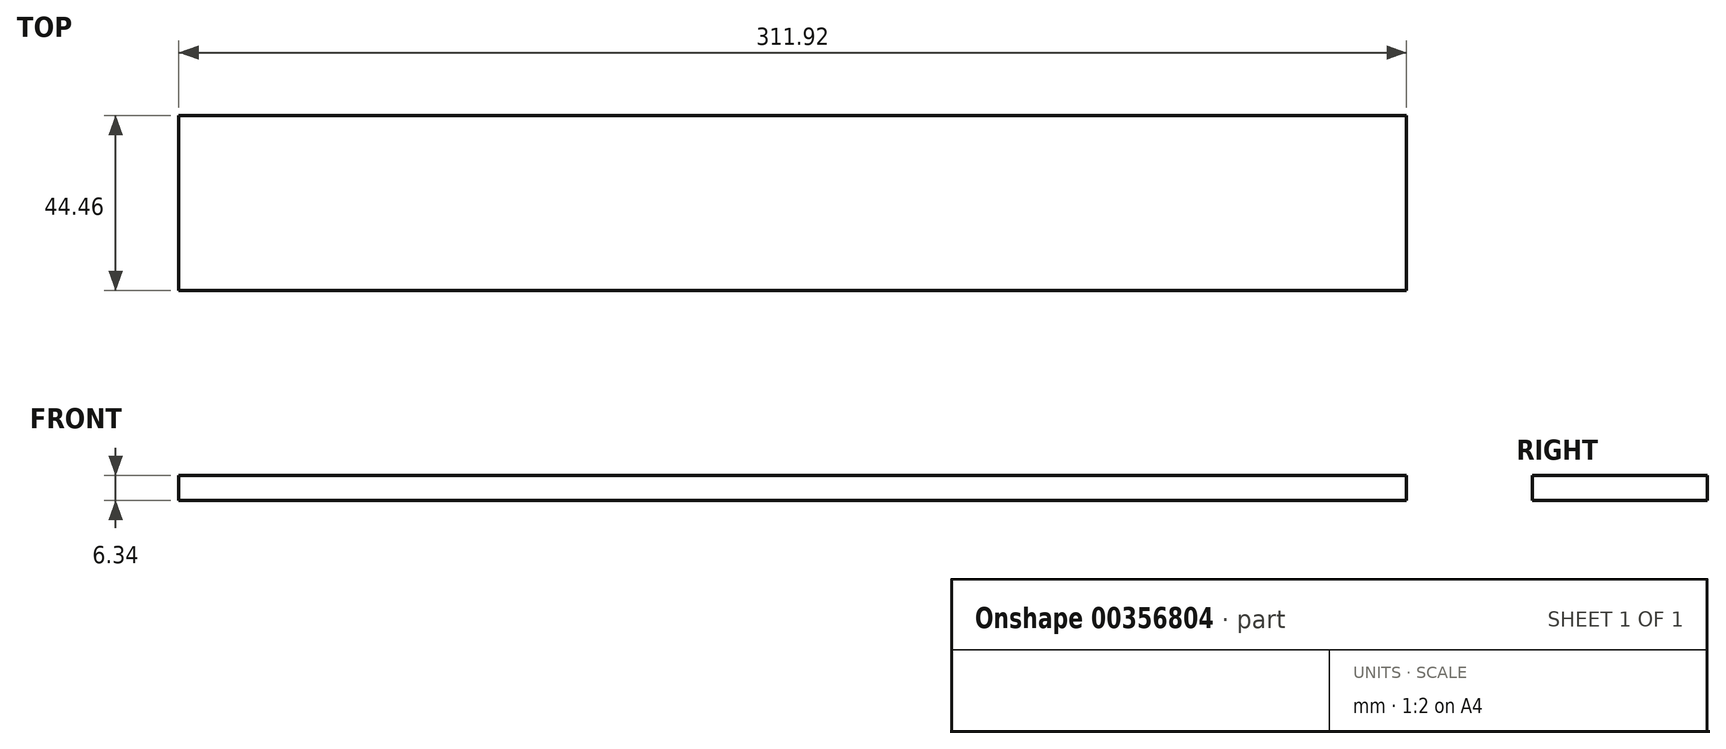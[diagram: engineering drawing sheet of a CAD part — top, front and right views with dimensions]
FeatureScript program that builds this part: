
annotation { "Feature Type Name" : "Feature", "Feature Type Description" : "" }
export const myFeature = defineFeature(function(context is Context, id is Id, definition is map)
    precondition{}
    {
        {
            var Q0;
            Q0=qCreatedBy(makeId("Front.planeOp"),FACE);
            var sketch = newSketch(context, id + "F0", { "sketchPlane" : qUnion([Q0])});
            skLineSegment(sketch, "E0.bottom", {"start": v(155.96, -3.17) * mm, "end": v(-155.96, -3.18) * mm});
            skLineSegment(sketch, "E0.top", {"start": v(155.96, 3.18) * mm, "end": v(-155.96, 3.17) * mm});
            skLineSegment(sketch, "E0.left", {"start": v(155.96, -3.17) * mm, "end": v(155.96, 3.18) * mm});
            skLineSegment(sketch, "E0.right", {"start": v(-155.96, -3.18) * mm, "end": v(-155.96, 3.17) * mm});
            skPoint(sketch, "E0.middle", {"position": v(0, 0) * mm});
            skSolve(sketch);
        }
        {
            var Q0;
            Q0 = qSketchRegion(id + "F0", true);
            extrude(context, id + "F1", {"entities" : qUnion([Q0]), "endBound" : BoundingType.SYMMETRIC, "depth" : 44.45 * mm});
        }
    });
